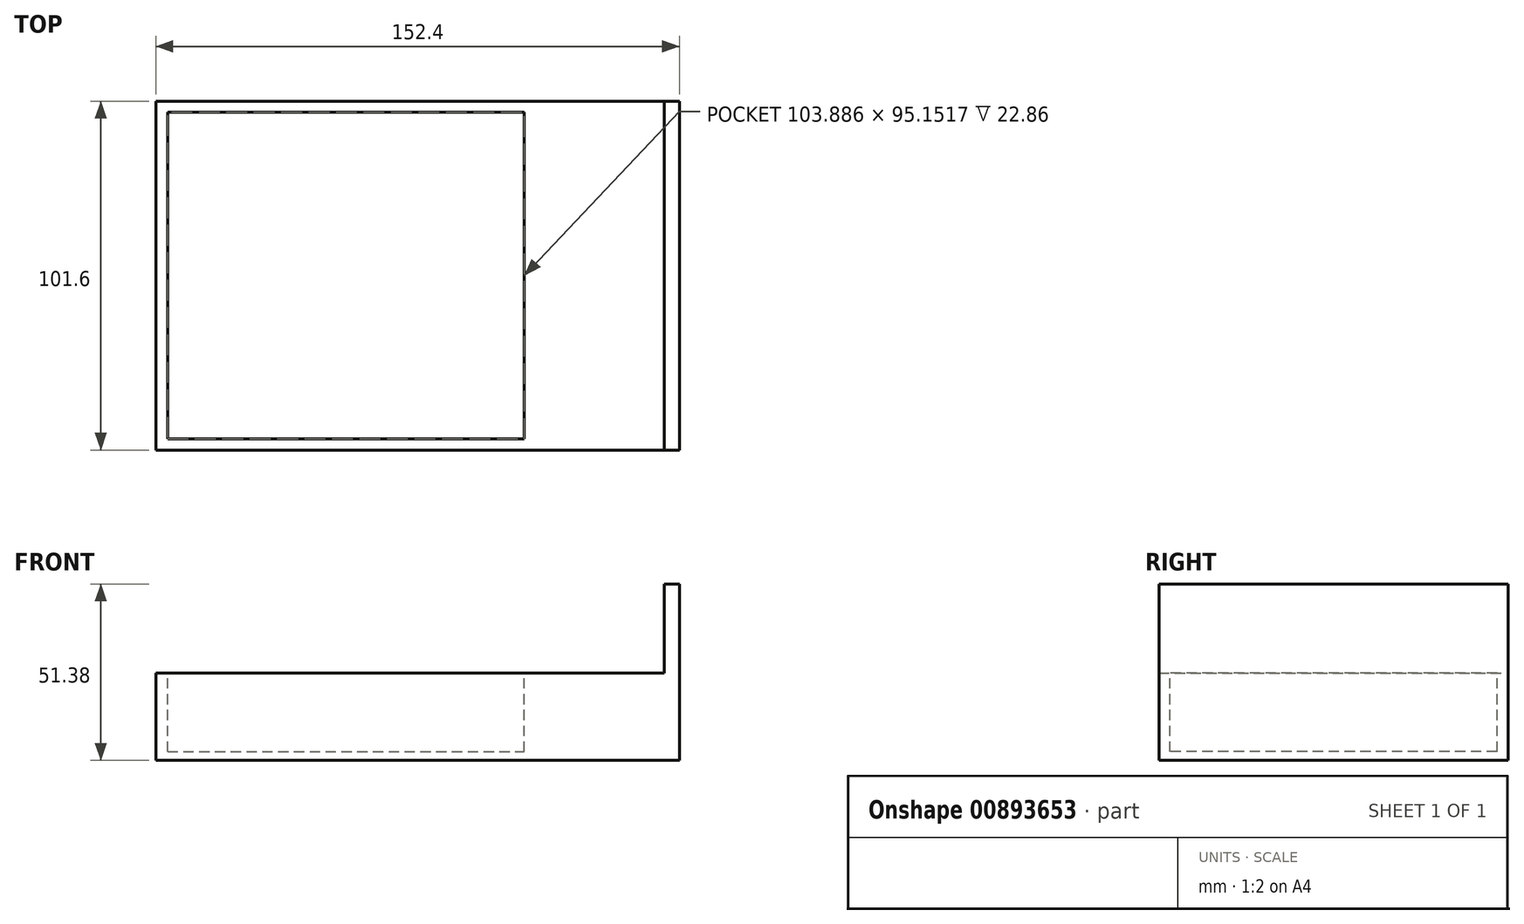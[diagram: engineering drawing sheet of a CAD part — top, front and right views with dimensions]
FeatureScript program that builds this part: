
annotation { "Feature Type Name" : "Feature", "Feature Type Description" : "" }
export const myFeature = defineFeature(function(context is Context, id is Id, definition is map)
    precondition{}
    {
        {
            var Q0;
            Q0=qCreatedBy(makeId("Front.planeOp"),FACE);
            var sketch = newSketch(context, id + "F0", { "sketchPlane" : qUnion([Q0])});
            skLineSegment(sketch, "E0", {"start": v(-55.96, 0) * mm, "end": v(96.44, 0) * mm});
            skLineSegment(sketch, "E1", {"start": v(96.44, 0) * mm, "end": v(96.44, 51.38) * mm});
            skLineSegment(sketch, "E2", {"start": v(96.44, 51.38) * mm, "end": v(92.08, 51.38) * mm});
            skLineSegment(sketch, "E3", {"start": v(92.08, 51.38) * mm, "end": v(92.08, 25.4) * mm});
            skLineSegment(sketch, "E4", {"start": v(92.08, 25.4) * mm, "end": v(-55.96, 25.4) * mm});
            skLineSegment(sketch, "E5", {"start": v(-55.96, 25.4) * mm, "end": v(-55.96, 0) * mm});
            skSolve(sketch);
        }
        {
            var Q0;
            Q0=makeQuery(id+"F0.imprint","IMPRINT",FACE,{"disambiguationData":[TD([[makeQuery(id+"F0.imprint","IMPRINT",EDGE,{"derivedFrom":sQuery(id+"F0.wireOp",EDGE,"E0")}),1.0]])]});
            extrude(context, id + "F1", {"entities" : qUnion([Q0]), "depth" : 101.6 * mm, "offsetDistance" : 25.4 * mm});
        }
        {
            var Q0;
            Q0=makeQuery(id+"F1.opExtrude","SWEPT_FACE",FACE,{"disambiguationData":[OSD([sQuery(id+"F0.wireOp",EDGE,"E4")])]});
            var sketch = newSketch(context, id + "F2", { "sketchPlane" : qUnion([Q0])});
            skLineSegment(sketch, "E6.bottom", {"start": v(-52.55, -3.21) * mm, "end": v(51.34, -3.21) * mm});
            skLineSegment(sketch, "E6.top", {"start": v(-52.55, -98.37) * mm, "end": v(51.34, -98.37) * mm});
            skLineSegment(sketch, "E6.left", {"start": v(-52.55, -3.21) * mm, "end": v(-52.55, -98.37) * mm});
            skLineSegment(sketch, "E6.right", {"start": v(51.34, -3.21) * mm, "end": v(51.34, -98.37) * mm});
            skSolve(sketch);
        }
        {
            var Q0;
            Q0 = qSketchRegion(id + "F2", true);
            extrude(context, id + "F3", {"entities" : qUnion([Q0]), "operationType" : NewBodyOperationType.REMOVE, "oppositeDirection" : true, "depth" : 22.86 * mm, "offsetDistance" : 25.4 * mm});
        }
    });
